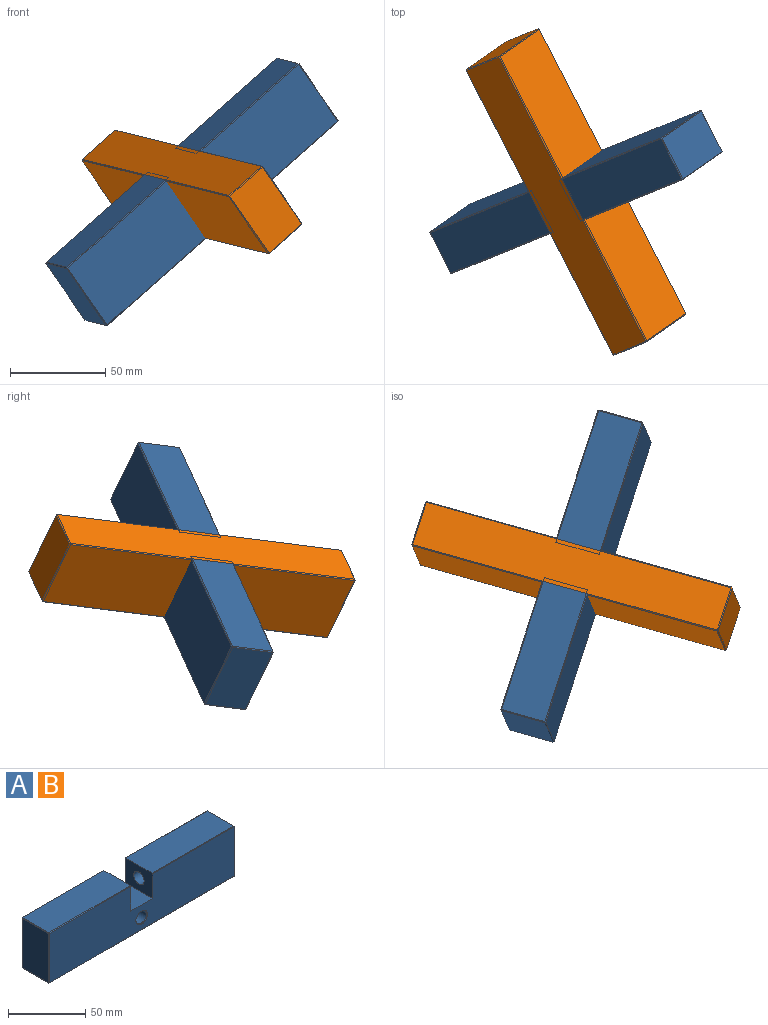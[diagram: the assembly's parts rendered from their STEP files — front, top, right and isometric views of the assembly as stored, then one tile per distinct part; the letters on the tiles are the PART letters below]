
ASSEMBLY  parts=2 mates=1
PART A: 39 faces, bbox 170x25x40 mm
  f0: plane 25x20mm, normal (1,0,0), area 428.9mm2, adj f1,f8,f9,f10,f11,f17,f23
  f1: plane 74.5x24mm, normal (0,0,1), area 1788mm2, adj f0,f17,f23,f24
  f2: plane 39x24mm, normal (-1,0,0), area 936mm2, adj f24,f25,f33,f34
  f3: plane 169x24mm, normal (0,0,-1), area 4056mm2, adj f26,f31,f34,f37
  f4: plane 39x24mm, normal (1,0,0), area 936mm2, adj f20,f21,f31,f32
  f5: plane 74.5x24mm, normal (0,0,1), area 1788mm2, adj f6,f16,f21,f22
  f6: plane 25x20mm, normal (-1,0,0), area 428.9mm2, adj f5,f8,f9,f10,f13,f16,f22
  f7: cylinder r=4.75mm len=24mm, axis (0,1,0), area 716.3mm2, adj f15,f38
  f8: plane 25x20mm, normal (0,0,1), area 500mm2, adj f0,f6,f9,f10
  f9: plane 169x39mm, normal (0,-1,0), area 6114.4mm2, adj f0,f6,f8,f16,f17,f20,f25,f26
  f10: plane 169x39mm, normal (0,1,0), area 6114.4mm2, adj f0,f6,f8,f15,f22,f23,f32,f33
  f11: cylinder r=4.75mm len=20mm, axis (1,0,0), area 596.9mm2, adj f0,f12
  f12: plane 9.5x9.5mm, normal (1,0,0), area 70.9mm2, adj f11
  f13: cylinder r=4.75mm len=20mm, axis (-1,0,0), area 596.9mm2, adj f6,f14
  f14: plane 9.5x9.5mm, normal (-1,0,0), area 70.9mm2, adj f13
  f15: cone r=5.25mm half-angle=45deg, axis (0,1,0), area 22.2mm2, adj f7,f10
  f16: plane 74.5x0.5mm, normal (0,-0.71,0.71), area 52.7mm2, adj f5,f6,f9,f18
  f17: plane 74.5x0.5mm, normal (0,-0.71,0.71), area 52.7mm2, adj f0,f1,f9,f19
  f18: plane 0.5x0.5mm, normal (0.58,-0.58,0.58), area 0.2mm2, adj f16,f20,f21
  f19: plane 0.5x0.5mm, normal (-0.58,-0.58,0.58), area 0.2mm2, adj f17,f24,f25
  f20: plane 39x0.5mm, normal (0.71,-0.71,0), area 27.6mm2, adj f4,f9,f18,f27
  f21: plane 24x0.5mm, normal (0.71,0,0.71), area 17mm2, adj f4,f5,f18,f28
  f22: plane 74.5x0.5mm, normal (0,0.71,0.71), area 52.7mm2, adj f5,f6,f10,f28
  f23: plane 74.5x0.5mm, normal (0,0.71,0.71), area 52.7mm2, adj f0,f1,f10,f29
  f24: plane 24x0.5mm, normal (-0.71,0,0.71), area 17mm2, adj f1,f2,f19,f29
  f25: plane 39x0.5mm, normal (-0.71,-0.71,0), area 27.6mm2, adj f2,f9,f19,f30
  f26: plane 169x0.5mm, normal (0,-0.71,-0.71), area 119.5mm2, adj f3,f9,f27,f30
  f27: plane 0.5x0.5mm, normal (0.58,-0.58,-0.58), area 0.2mm2, adj f20,f26,f31
  f28: plane 0.5x0.5mm, normal (0.58,0.58,0.58), area 0.2mm2, adj f21,f22,f32
  f29: plane 0.5x0.5mm, normal (-0.58,0.58,0.58), area 0.2mm2, adj f23,f24,f33
  f30: plane 0.5x0.5mm, normal (-0.58,-0.58,-0.58), area 0.2mm2, adj f25,f26,f34
  f31: plane 24x0.5mm, normal (0.71,0,-0.71), area 17mm2, adj f3,f4,f27,f35
  f32: plane 39x0.5mm, normal (0.71,0.71,0), area 27.6mm2, adj f4,f10,f28,f35
  f33: plane 39x0.5mm, normal (-0.71,0.71,0), area 27.6mm2, adj f2,f10,f29,f36
  f34: plane 24x0.5mm, normal (-0.71,0,-0.71), area 17mm2, adj f2,f3,f30,f36
  f35: plane 0.5x0.5mm, normal (0.58,0.58,-0.58), area 0.2mm2, adj f31,f32,f37
  f36: plane 0.5x0.5mm, normal (-0.58,0.58,-0.58), area 0.2mm2, adj f33,f34,f37
  f37: plane 169x0.5mm, normal (0,0.71,-0.71), area 119.5mm2, adj f3,f10,f35,f36
  f38: cone r=4.75mm half-angle=45deg, axis (0,-1,0), area 22.2mm2, adj f7,f9
PART B: same geometry as A
PLACE A rot(axis=(0.33,-0.79,0.51),46.9deg) t=(-6.02,97.2,259.52)mm
PLACE B rot(axis=(0.51,0.8,0.32),165deg) t=(8.65,89.79,266.04)mm
MATE fastened B.f8 <-> A.f8  axis (0.53,0.37,-0.77) through (-0.32,86.16,258.13)mm
